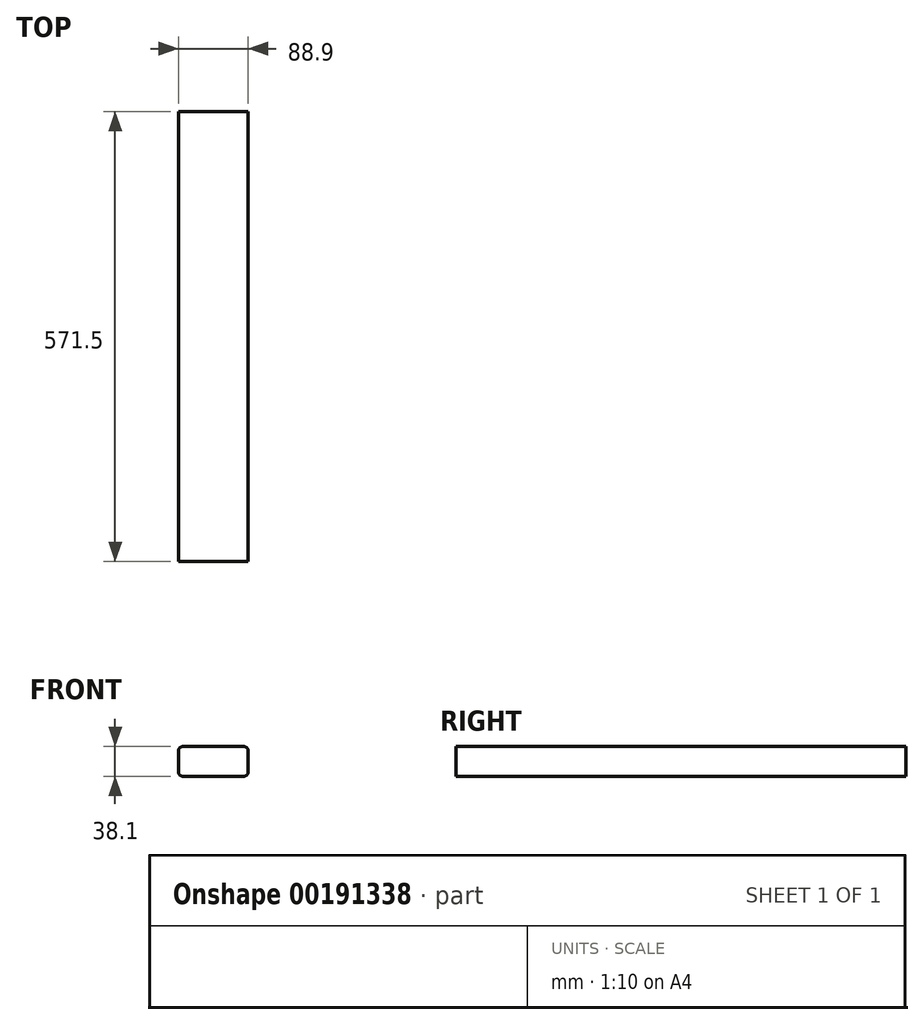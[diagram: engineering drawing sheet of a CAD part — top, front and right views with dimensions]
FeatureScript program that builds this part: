
annotation { "Feature Type Name" : "Feature", "Feature Type Description" : "" }
export const myFeature = defineFeature(function(context is Context, id is Id, definition is map)
    precondition{}
    {
        {
            var Q0;
            Q0=qCreatedBy(makeId("Front.planeOp"),FACE);
            var sketch = newSketch(context, id + "F0", { "sketchPlane" : qUnion([Q0])});
            skLineSegment(sketch, "E0.bottom", {"start": v(-38.1, 19.05) * mm, "end": v(38.1, 19.05) * mm});
            skLineSegment(sketch, "E0.top", {"start": v(-38.1, -19.05) * mm, "end": v(38.1, -19.05) * mm});
            skLineSegment(sketch, "E0.left", {"start": v(-44.45, 12.7) * mm, "end": v(-44.45, -12.7) * mm});
            skLineSegment(sketch, "E0.right", {"start": v(44.45, 12.7) * mm, "end": v(44.45, -12.7) * mm});
            skPoint(sketch, "E0.middle", {"position": v(0, 0) * mm});
            skPoint(sketch, "E1.visualSharp", {"position": v(-44.45, 19.05) * mm});
            skArc(sketch, "E1.filletArc", {"start": v(-38.1, 19.05) * mm, "mid": v(-42.6, 17.2) * mm, "end": v(-44.45, 12.7) * mm});
            skPoint(sketch, "E2.visualSharp", {"position": v(-44.45, -19.05) * mm});
            skArc(sketch, "E2.filletArc", {"start": v(-44.45, -12.7) * mm, "mid": v(-42.6, -17.2) * mm, "end": v(-38.1, -19.05) * mm});
            skPoint(sketch, "E3.visualSharp", {"position": v(44.45, 19.05) * mm});
            skArc(sketch, "E3.filletArc", {"start": v(44.45, 12.7) * mm, "mid": v(42.6, 17.2) * mm, "end": v(38.1, 19.05) * mm});
            skPoint(sketch, "E4.visualSharp", {"position": v(44.45, -19.05) * mm});
            skArc(sketch, "E4.filletArc", {"start": v(38.1, -19.05) * mm, "mid": v(42.6, -17.2) * mm, "end": v(44.45, -12.7) * mm});
            skSolve(sketch);
        }
        {
            var Q0;
            Q0=makeQuery(id+"F0.imprint","IMPRINT",FACE,{"disambiguationData":[TD([[makeQuery(id+"F0.imprint","IMPRINT",EDGE,{"derivedFrom":sQuery(id+"F0.wireOp",EDGE,"E0.bottom")}),-1.0]])]});
            extrude(context, id + "F1", {"entities" : qUnion([Q0]), "depth" : 571.5 * mm});
        }
    });
